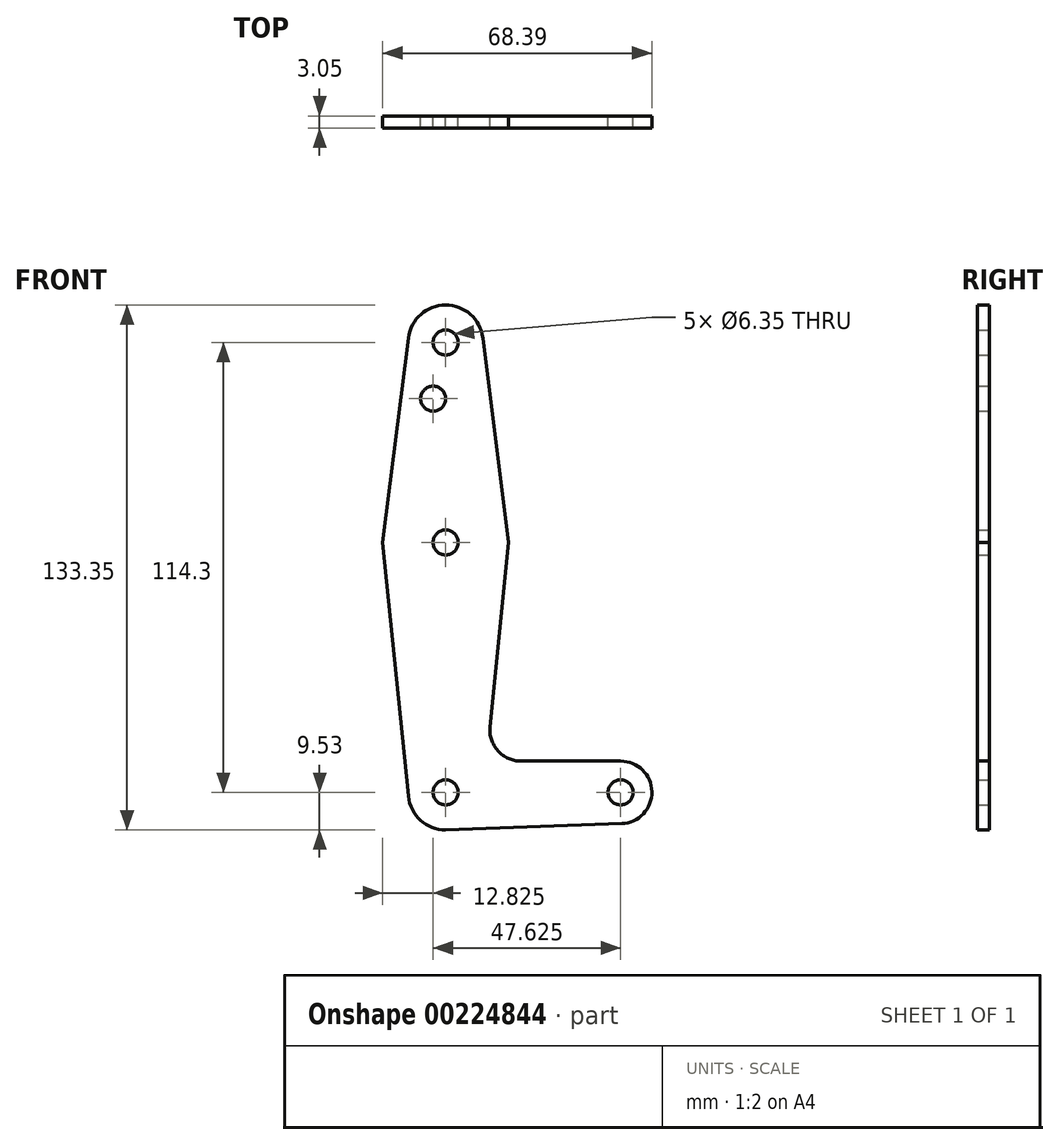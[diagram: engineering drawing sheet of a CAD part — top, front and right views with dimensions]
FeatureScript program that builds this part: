
annotation { "Feature Type Name" : "Feature", "Feature Type Description" : "" }
export const myFeature = defineFeature(function(context is Context, id is Id, definition is map)
    precondition{}
    {
        {
            var Q0;
            Q0=qCreatedBy(makeId("Front.planeOp"),FACE);
            var sketch = newSketch(context, id + "F0", { "sketchPlane" : qUnion([Q0])});
            skLineSegment(sketch, "E0", {"start": v(0, -63.5) * mm, "end": v(0, 50.8) * mm});
            skLineSegment(sketch, "E1", {"start": v(0, -63.5) * mm, "end": v(44.45, -63.5) * mm});
            skCircle(sketch, "E2", {"center": v(44.45, -63.5) * mm, "radius": 7.94 * mm});
            skCircle(sketch, "E3", {"center": v(0, -63.5) * mm, "radius": 9.52 * mm});
            skCircle(sketch, "E4", {"center": v(0, 0) * mm, "radius": 15.88 * mm});
            skCircle(sketch, "E5", {"center": v(0, 50.8) * mm, "radius": 9.53 * mm});
            skLineSegment(sketch, "E6", {"start": v(9.45, 52) * mm, "end": v(16, 0) * mm});
            skLineSegment(sketch, "E7", {"start": v(-9.45, 52) * mm, "end": v(-16, 0) * mm});
            skLineSegment(sketch, "E8", {"start": v(-9.48, -64.46) * mm, "end": v(-16, 0) * mm});
            skLineSegment(sketch, "E9", {"start": v(16, 0) * mm, "end": v(11.26, -46.81) * mm});
            skLineSegment(sketch, "E10", {"start": v(19.17, -55.56) * mm, "end": v(44.45, -55.56) * mm});
            skLineSegment(sketch, "E11", {"start": v(0, -73.03) * mm, "end": v(44.73, -71.43) * mm});
            skCircle(sketch, "E12", {"center": v(0, 50.8) * mm, "radius": 3.18 * mm});
            skCircle(sketch, "E13", {"center": v(-3.18, 36.53) * mm, "radius": 3.18 * mm});
            skCircle(sketch, "E14", {"center": v(0, 0) * mm, "radius": 3.18 * mm});
            skCircle(sketch, "E15", {"center": v(0, -63.5) * mm, "radius": 3.18 * mm});
            skCircle(sketch, "E16", {"center": v(44.45, -63.5) * mm, "radius": 3.18 * mm});
            skPoint(sketch, "E17.newPointB", {"position": v(0, -55.56) * mm});
            skArc(sketch, "E17.filletArc", {"start": v(11.26, -46.81) * mm, "mid": v(13.27, -52.94) * mm, "end": v(19.17, -55.56) * mm});
            skSolve(sketch);
        }
        {
            var Q0;
            Q0=makeQuery(id+"F0.imprint","IMPRINT",FACE,{"disambiguationData":[TD([[makeQuery(id+"F0.imprint","IMPRINT",EDGE,{"derivedFrom":sQuery(id+"F0.wireOp",EDGE,"E12")}),-1.0]])]});
            var Q1;
            {var subQ5=sQuery(id+"F0.wireOp",EDGE,"E13");Q1=makeQuery(id+"F0.imprint","IMPRINT",FACE,{"disambiguationData":[TD([[makeQuery(id+"F0.imprint","IMPRINT",EDGE,{"derivedFrom":subQ5}),-1.0]])]});}
            var Q2;
            {var subQ3=sQuery(id+"F0.wireOp",EDGE,"E0");var subQ5=makeQuery(id+"F0.imprint","INTERSECT",VERTEX,{"derivedFrom":[subQ3,sQuery(id+"F0.wireOp",EDGE,"E13")]});Q2=makeQuery(id+"F0.imprint","IMPRINT",FACE,{"disambiguationData":[TD([[makeQuery(id+"F0.imprint","IMPRINT",EDGE,{"disambiguationData":[TD([[subQ5,1.0]])],"derivedFrom":subQ3}),-1.0]])]});}
            var Q3;
            {var subQ0=sQuery(id+"F0.wireOp",EDGE,"E4");var subQ2=sQuery(id+"F0.wireOp",EDGE,"E0");var subQ3=makeQuery(id+"F0.imprint","INTERSECT",VERTEX,{"disambiguationData":[OD(0.0)],"derivedFrom":[subQ2,subQ0]});Q3=makeQuery(id+"F0.imprint","IMPRINT",FACE,{"disambiguationData":[TD([[makeQuery(id+"F0.imprint","IMPRINT",EDGE,{"disambiguationData":[TD([[subQ3,-1.0]])],"derivedFrom":subQ2}),1.0]])]});}
            var Q4;
            {var subQ0=sQuery(id+"F0.wireOp",EDGE,"E4");var subQ2=sQuery(id+"F0.wireOp",EDGE,"E0");var subQ3=makeQuery(id+"F0.imprint","INTERSECT",VERTEX,{"disambiguationData":[OD(0.0)],"derivedFrom":[subQ2,subQ0]});Q4=makeQuery(id+"F0.imprint","IMPRINT",FACE,{"disambiguationData":[TD([[makeQuery(id+"F0.imprint","IMPRINT",EDGE,{"disambiguationData":[TD([[subQ3,-1.0]])],"derivedFrom":subQ2}),-1.0]])]});}
            var Q5;
            {var subQ5=sQuery(id+"F0.wireOp",EDGE,"E8");Q5=makeQuery(id+"F0.imprint","IMPRINT",FACE,{"disambiguationData":[TD([[makeQuery(id+"F0.imprint","IMPRINT",EDGE,{"derivedFrom":subQ5}),-1.0]])]});}
            var Q6;
            {var subQ12=sQuery(id+"F0.wireOp",EDGE,"E9");Q6=makeQuery(id+"F0.imprint","IMPRINT",FACE,{"disambiguationData":[TD([[makeQuery(id+"F0.imprint","IMPRINT",EDGE,{"derivedFrom":subQ12}),-1.0]])]});}
            var Q7;
            {var subQ0=sQuery(id+"F0.wireOp",EDGE,"E15");var subQ1=sQuery(id+"F0.wireOp",EDGE,"E0");var subQ2=makeQuery(id+"F0.imprint","INTERSECT",VERTEX,{"derivedFrom":[subQ1,subQ0]});Q7=makeQuery(id+"F0.imprint","IMPRINT",FACE,{"disambiguationData":[TD([[makeQuery(id+"F0.imprint","IMPRINT",EDGE,{"disambiguationData":[TD([[subQ2,-1.0]])],"derivedFrom":subQ1}),-1.0]])]});}
            var Q8;
            {var subQ2=sQuery(id+"F0.wireOp",EDGE,"E0");var subQ4=sQuery(id+"F0.wireOp",EDGE,"E15");var subQ11=makeQuery(id+"F0.imprint","INTERSECT",VERTEX,{"derivedFrom":[subQ2,subQ4]});Q8=makeQuery(id+"F0.imprint","IMPRINT",FACE,{"disambiguationData":[TD([[makeQuery(id+"F0.imprint","IMPRINT",EDGE,{"disambiguationData":[TD([[subQ11,-1.0]])],"derivedFrom":subQ2}),1.0]])]});}
            var Q9;
            {var subQ0=sQuery(id+"F0.wireOp",EDGE,"E2");var subQ1=sQuery(id+"F0.wireOp",EDGE,"E1");var subQ2=makeQuery(id+"F0.imprint","INTERSECT",VERTEX,{"derivedFrom":[subQ1,subQ0]});Q9=makeQuery(id+"F0.imprint","IMPRINT",FACE,{"disambiguationData":[TD([[makeQuery(id+"F0.imprint","IMPRINT",EDGE,{"disambiguationData":[TD([[subQ2,1.0]])],"derivedFrom":subQ1}),-1.0]])]});}
            var Q10;
            Q10=makeQuery(id+"F0.imprint","IMPRINT",FACE,{"disambiguationData":[TD([[makeQuery(id+"F0.imprint","IMPRINT",EDGE,{"derivedFrom":sQuery(id+"F0.wireOp",EDGE,"E16")}),-1.0]])]});
            extrude(context, id + "F1", {"entities" : qUnion([Q0, Q1, Q2, Q3, Q4, Q5, Q6, Q7, Q8, Q9, Q10]), "depth" : 3.05 * mm});
        }
    });
